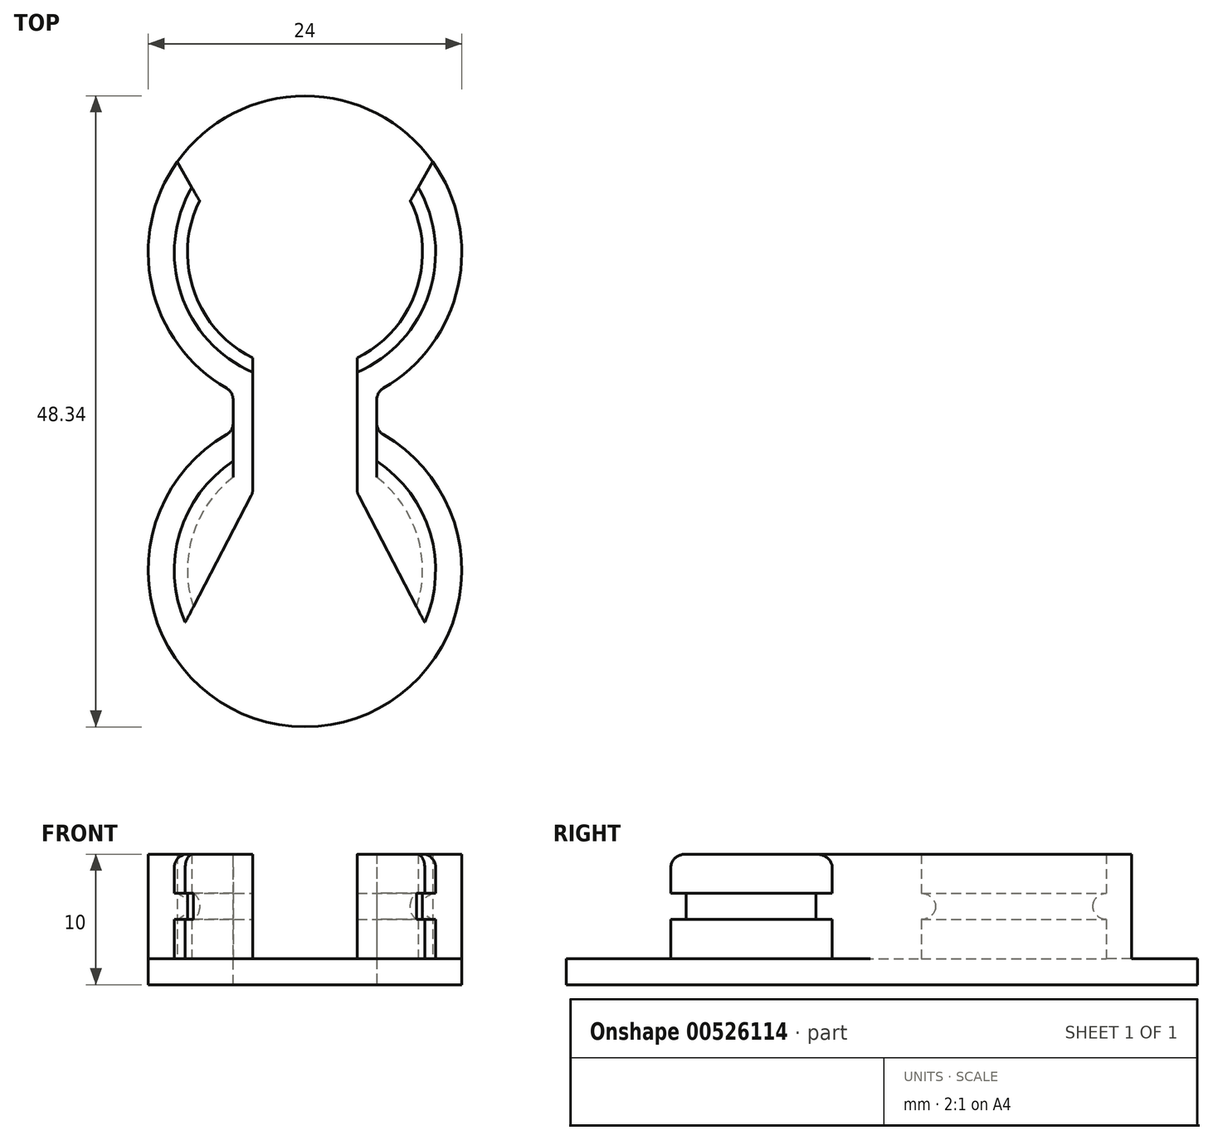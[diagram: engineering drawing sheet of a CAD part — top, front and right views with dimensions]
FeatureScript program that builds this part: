
annotation { "Feature Type Name" : "Feature", "Feature Type Description" : "" }
export const myFeature = defineFeature(function(context is Context, id is Id, definition is map)
    precondition{}
    {
        {
            var Q0;
            Q0=qCreatedBy(makeId("Top.planeOp"),FACE);
            var sketch = newSketch(context, id + "F0", { "sketchPlane" : qUnion([Q0])});
            skArc(sketch, "E0", {"start": v(-5.5, 1.5) * mm, "mid": v(0, 24.17) * mm, "end": v(5.5, 1.5) * mm});
            skArc(sketch, "E1", {"start": v(-5.5, -1.5) * mm, "mid": v(0, -24.17) * mm, "end": v(5.5, -1.5) * mm});
            skLineSegment(sketch, "E2", {"start": v(-5.5, 1.5) * mm, "end": v(-5.5, -1.5) * mm});
            skLineSegment(sketch, "E3", {"start": v(5.5, 1.5) * mm, "end": v(5.5, -1.5) * mm});
            skSolve(sketch);
        }
        {
            var Q0;
            Q0 = qSketchRegion(id + "F0", true);
            extrude(context, id + "F1", {"entities" : qUnion([Q0]), "depth" : 2 * mm, "offsetDistance" : 25 * mm});
        }
        {
            var Q0;
            Q0=makeQuery(id+"F1.opExtrude","CAP_FACE",FACE,{"disambiguationData":[OSD([sQuery(id+"F0.wireOp",EDGE,"E0"),sQuery(id+"F0.wireOp",EDGE,"E1"),sQuery(id+"F0.wireOp",EDGE,"E2"),sQuery(id+"F0.wireOp",EDGE,"E3")])],"isStart":false});
            var sketch = newSketch(context, id + "F2", { "sketchPlane" : qUnion([Q0])});
            skArc(sketch, "E4", {"start": v(8.66, 17.17) * mm, "mid": v(9.5, 9.04) * mm, "end": v(4, 3) * mm});
            skArc(sketch, "E5", {"start": v(9.78, 19.11) * mm, "mid": v(11.66, 9.33) * mm, "end": v(5.5, 1.5) * mm});
            skArc(sketch, "E6", {"start": v(-8.66, 17.17) * mm, "mid": v(-9.5, 9.04) * mm, "end": v(-4, 3) * mm});
            skArc(sketch, "E7", {"start": v(5.5, -3.81) * mm, "mid": v(9.59, -9.32) * mm, "end": v(9.17, -16.17) * mm});
            skLineSegment(sketch, "E8", {"start": v(9.78, 19.11) * mm, "end": v(8.66, 17.17) * mm});
            skLineSegment(sketch, "E9", {"start": v(-8.66, 17.17) * mm, "end": v(-9.78, 19.11) * mm});
            skLineSegment(sketch, "E10", {"start": v(5.5, 1.5) * mm, "end": v(5.5, -3.81) * mm});
            skLineSegment(sketch, "E11", {"start": v(-4, 3) * mm, "end": v(-4, -6.24) * mm});
            skLineSegment(sketch, "E12", {"start": v(-4, -6.24) * mm, "end": v(-9.17, -16.17) * mm});
            skLineSegment(sketch, "E13", {"start": v(9.17, -16.17) * mm, "end": v(4, -6.24) * mm});
            skLineSegment(sketch, "E14", {"start": v(4, -6.24) * mm, "end": v(4, 3) * mm});
            skArc(sketch, "E15", {"start": v(-9.78, 19.11) * mm, "mid": v(-11.66, 9.33) * mm, "end": v(-5.5, 1.5) * mm});
            skArc(sketch, "E16", {"start": v(-9.17, -16.17) * mm, "mid": v(-9.59, -9.32) * mm, "end": v(-5.5, -3.81) * mm});
            skLineSegment(sketch, "E17", {"start": v(-5.5, 1.5) * mm, "end": v(-5.5, -3.81) * mm});
            skArc(sketch, "E18.0", {"start": v(-5.5, 1.5) * mm, "mid": v(0, 24.17) * mm, "end": v(5.5, 1.5) * mm, "construction": true});
            skArc(sketch, "E19.0", {"start": v(-5.5, -1.5) * mm, "mid": v(0, -24.17) * mm, "end": v(5.5, -1.5) * mm, "construction": true});
            skSolve(sketch);
        }
        {
            var Q0;
            Q0 = qSketchRegion(id + "F2", true);
            extrude(context, id + "F3", {"entities" : qUnion([Q0]), "operationType" : NewBodyOperationType.ADD, "depth" : 3 * mm, "offsetDistance" : 25 * mm});
        }
        {
            var Q0;
            Q0=makeQuery(id+"F3.opExtrude","CAP_FACE",FACE,{"disambiguationData":[OSD([sQuery(id+"F2.wireOp",EDGE,"E4"),sQuery(id+"F2.wireOp",EDGE,"E5"),sQuery(id+"F2.wireOp",EDGE,"E7"),sQuery(id+"F2.wireOp",EDGE,"E8"),sQuery(id+"F2.wireOp",EDGE,"E10"),sQuery(id+"F2.wireOp",EDGE,"E13"),sQuery(id+"F2.wireOp",EDGE,"E14")])],"isStart":false});
            var sketch = newSketch(context, id + "F4", { "sketchPlane" : qUnion([Q0])});
            skArc(sketch, "E20", {"start": v(-9.78, 19.11) * mm, "mid": v(-11.66, 9.33) * mm, "end": v(-5.5, 1.5) * mm});
            skArc(sketch, "E21", {"start": v(9.78, 19.11) * mm, "mid": v(11.66, 9.33) * mm, "end": v(5.5, 1.5) * mm});
            skArc(sketch, "E22", {"start": v(8.07, 16.15) * mm, "mid": v(8.53, 9.28) * mm, "end": v(4, 4.1) * mm});
            skArc(sketch, "E23", {"start": v(-8.07, 16.15) * mm, "mid": v(-8.53, 9.28) * mm, "end": v(-4, 4.1) * mm});
            skArc(sketch, "E24", {"start": v(5.5, -5.04) * mm, "mid": v(8.6, -9.53) * mm, "end": v(8.55, -14.98) * mm});
            skArc(sketch, "E25", {"start": v(-5.5, -5.04) * mm, "mid": v(-8.6, -9.53) * mm, "end": v(-8.55, -14.98) * mm});
            skLineSegment(sketch, "E26", {"start": v(-5.5, 1.5) * mm, "end": v(-5.5, -5.04) * mm});
            skLineSegment(sketch, "E27", {"start": v(5.5, 1.5) * mm, "end": v(5.5, -5.04) * mm});
            skLineSegment(sketch, "E28", {"start": v(-4, 4.1) * mm, "end": v(-4, -6.24) * mm});
            skLineSegment(sketch, "E29", {"start": v(-4, -6.24) * mm, "end": v(-8.55, -14.98) * mm});
            skLineSegment(sketch, "E30", {"start": v(4, 4.1) * mm, "end": v(4, -6.24) * mm});
            skLineSegment(sketch, "E31", {"start": v(4, -6.24) * mm, "end": v(8.55, -14.98) * mm});
            skLineSegment(sketch, "E32", {"start": v(8.07, 16.15) * mm, "end": v(9.78, 19.11) * mm});
            skLineSegment(sketch, "E33", {"start": v(-9.78, 19.11) * mm, "end": v(-8.07, 16.15) * mm});
            skLineSegment(sketch, "E34.0", {"start": v(-8.66, 17.17) * mm, "end": v(-9.78, 19.11) * mm, "construction": true});
            skLineSegment(sketch, "E35.0", {"start": v(9.78, 19.11) * mm, "end": v(8.66, 17.17) * mm, "construction": true});
            skLineSegment(sketch, "E36.0", {"start": v(-4, -6.24) * mm, "end": v(-9.17, -16.17) * mm, "construction": true});
            skLineSegment(sketch, "E37.0", {"start": v(9.17, -16.17) * mm, "end": v(4, -6.24) * mm, "construction": true});
            skArc(sketch, "E38.0", {"start": v(-9.78, 19.11) * mm, "mid": v(0, 24.17) * mm, "end": v(9.78, 19.11) * mm, "construction": true});
            skArc(sketch, "E39.0", {"start": v(-5.5, -1.5) * mm, "mid": v(0, -24.17) * mm, "end": v(5.5, -1.5) * mm, "construction": true});
            skSolve(sketch);
        }
        {
            var Q0;
            Q0 = qSketchRegion(id + "F4", true);
            extrude(context, id + "F5", {"entities" : qUnion([Q0]), "operationType" : NewBodyOperationType.ADD, "depth" : 2 * mm, "offsetDistance" : 25 * mm});
        }
        {
            var Q0;
            Q0=makeQuery(id+"F5.opExtrude","CAP_FACE",FACE,{"disambiguationData":[OSD([sQuery(id+"F4.wireOp",EDGE,"E21"),sQuery(id+"F4.wireOp",EDGE,"E22"),sQuery(id+"F4.wireOp",EDGE,"E24"),sQuery(id+"F4.wireOp",EDGE,"E27"),sQuery(id+"F4.wireOp",EDGE,"E30"),sQuery(id+"F4.wireOp",EDGE,"E31"),sQuery(id+"F4.wireOp",EDGE,"E32")])],"isStart":false});
            var sketch = newSketch(context, id + "F6", { "sketchPlane" : qUnion([Q0])});
            skArc(sketch, "E40", {"start": v(8.66, 17.17) * mm, "mid": v(9.5, 9.04) * mm, "end": v(4, 3) * mm});
            skArc(sketch, "E41", {"start": v(9.78, 19.11) * mm, "mid": v(11.66, 9.33) * mm, "end": v(5.5, 1.5) * mm});
            skArc(sketch, "E42", {"start": v(-8.66, 17.17) * mm, "mid": v(-9.5, 9.04) * mm, "end": v(-4, 3) * mm});
            skArc(sketch, "E43", {"start": v(5.5, -3.81) * mm, "mid": v(9.59, -9.32) * mm, "end": v(9.17, -16.17) * mm});
            skLineSegment(sketch, "E44", {"start": v(9.78, 19.11) * mm, "end": v(8.66, 17.17) * mm});
            skLineSegment(sketch, "E45", {"start": v(-8.66, 17.17) * mm, "end": v(-9.78, 19.11) * mm});
            skLineSegment(sketch, "E46", {"start": v(5.5, 1.5) * mm, "end": v(5.5, -3.81) * mm});
            skLineSegment(sketch, "E47", {"start": v(-4, 3) * mm, "end": v(-4, -6.24) * mm});
            skLineSegment(sketch, "E48", {"start": v(-4, -6.24) * mm, "end": v(-9.17, -16.17) * mm});
            skLineSegment(sketch, "E49", {"start": v(9.17, -16.17) * mm, "end": v(4, -6.24) * mm});
            skLineSegment(sketch, "E50", {"start": v(4, -6.24) * mm, "end": v(4, 3) * mm});
            skArc(sketch, "E51", {"start": v(-9.78, 19.11) * mm, "mid": v(-11.66, 9.33) * mm, "end": v(-5.5, 1.5) * mm});
            skArc(sketch, "E52", {"start": v(-9.17, -16.17) * mm, "mid": v(-9.59, -9.32) * mm, "end": v(-5.5, -3.81) * mm});
            skLineSegment(sketch, "E53", {"start": v(-5.5, 1.5) * mm, "end": v(-5.5, -3.81) * mm});
            skArc(sketch, "E54.0", {"start": v(-5.5, -1.5) * mm, "mid": v(0, -24.17) * mm, "end": v(5.5, -1.5) * mm, "construction": true});
            skArc(sketch, "E55.0", {"start": v(-9.78, 19.11) * mm, "mid": v(0, 24.17) * mm, "end": v(9.78, 19.11) * mm, "construction": true});
            skSolve(sketch);
        }
        {
            var Q0;
            Q0 = qSketchRegion(id + "F6", true);
            extrude(context, id + "F7", {"entities" : qUnion([Q0]), "operationType" : NewBodyOperationType.ADD, "depth" : 3 * mm, "offsetDistance" : 25 * mm});
        }
        {
            var Q0;
            Q0=makeQuery(id+"F5.opExtrude","CAP_EDGE",EDGE,{"disambiguationData":[OSD([sQuery(id+"F4.wireOp",EDGE,"E22")])],"isStart":false});
            var Q1;
            Q1=makeQuery(id+"F5.opExtrude","CAP_EDGE",EDGE,{"disambiguationData":[OSD([sQuery(id+"F4.wireOp",EDGE,"E23")])],"isStart":false});
            var Q2;
            Q2=makeQuery(id+"F5.opExtrude","CAP_EDGE",EDGE,{"disambiguationData":[OSD([sQuery(id+"F4.wireOp",EDGE,"E23")])],"isStart":true});
            var Q3;
            Q3=makeQuery(id+"F5.opExtrude","CAP_EDGE",EDGE,{"disambiguationData":[OSD([sQuery(id+"F4.wireOp",EDGE,"E22")])],"isStart":true});
            var Q4;
            Q4=makeQuery(id+"F5.opExtrude","CAP_EDGE",EDGE,{"disambiguationData":[OSD([sQuery(id+"F4.wireOp",EDGE,"E25")])],"isStart":true});
            var Q5;
            Q5=makeQuery(id+"F5.opExtrude","CAP_EDGE",EDGE,{"disambiguationData":[OSD([sQuery(id+"F4.wireOp",EDGE,"E25")])],"isStart":false});
            var Q6;
            Q6=makeQuery(id+"F5.opExtrude","CAP_EDGE",EDGE,{"disambiguationData":[OSD([sQuery(id+"F4.wireOp",EDGE,"E24")])],"isStart":false});
            var Q7;
            Q7=makeQuery(id+"F5.opExtrude","CAP_EDGE",EDGE,{"disambiguationData":[OSD([sQuery(id+"F4.wireOp",EDGE,"E24")])],"isStart":true});
            fillet(context, id + "F8", {"entities" : qUnion([Q0, Q1, Q2, Q3, Q4, Q5, Q6, Q7]), "radius" : 1 * mm, "tangentPropagation" : true, "allowEdgeOverflow" : false});
        }
        {
            var Q0;
            Q0=makeQuery(id+"F3.opExtrude","CAP_EDGE",EDGE,{"disambiguationData":[OSD([sQuery(id+"F2.wireOp",EDGE,"E11")])],"isStart":true});
            var Q1;
            Q1=makeQuery(id+"F3.opExtrude","CAP_EDGE",EDGE,{"disambiguationData":[OSD([sQuery(id+"F2.wireOp",EDGE,"E12")])],"isStart":true});
            var Q2;
            Q2=makeQuery(id+"F7.boolean.opBoolean","MERGE",EDGE,{"derivedFrom":[makeQuery(id+"F5.boolean.opBoolean","MERGE",EDGE,{"derivedFrom":[makeQuery(id+"F3.opExtrude","SWEPT_EDGE",EDGE,{"disambiguationData":[OSD([sQuery(id+"F2.wireOp",EDGE,"E11"),sQuery(id+"F2.wireOp",EDGE,"E12")])]}),makeQuery(id+"F5.opExtrude","SWEPT_EDGE",EDGE,{"disambiguationData":[OSD([sQuery(id+"F4.wireOp",EDGE,"E28"),sQuery(id+"F4.wireOp",EDGE,"E29")])]})]}),makeQuery(id+"F7.opExtrude","SWEPT_EDGE",EDGE,{"disambiguationData":[OSD([sQuery(id+"F6.wireOp",EDGE,"E47"),sQuery(id+"F6.wireOp",EDGE,"E48")])]})]});
            var Q3;
            Q3=makeQuery(id+"F3.opExtrude","CAP_EDGE",EDGE,{"disambiguationData":[OSD([sQuery(id+"F2.wireOp",EDGE,"E13")])],"isStart":true});
            var Q4;
            Q4=makeQuery(id+"F3.opExtrude","CAP_EDGE",EDGE,{"disambiguationData":[OSD([sQuery(id+"F2.wireOp",EDGE,"E14")])],"isStart":true});
            var Q5;
            Q5=makeQuery(id+"F7.boolean.opBoolean","MERGE",EDGE,{"derivedFrom":[makeQuery(id+"F5.boolean.opBoolean","MERGE",EDGE,{"derivedFrom":[makeQuery(id+"F3.opExtrude","SWEPT_EDGE",EDGE,{"disambiguationData":[OSD([sQuery(id+"F2.wireOp",EDGE,"E13"),sQuery(id+"F2.wireOp",EDGE,"E14")])]}),makeQuery(id+"F5.opExtrude","SWEPT_EDGE",EDGE,{"disambiguationData":[OSD([sQuery(id+"F4.wireOp",EDGE,"E30"),sQuery(id+"F4.wireOp",EDGE,"E31")])]})]}),makeQuery(id+"F7.opExtrude","SWEPT_EDGE",EDGE,{"disambiguationData":[OSD([sQuery(id+"F6.wireOp",EDGE,"E49"),sQuery(id+"F6.wireOp",EDGE,"E50")])]})]});
            var Q6;
            Q6=makeQuery(id+"F7.opExtrude","CAP_EDGE",EDGE,{"disambiguationData":[OSD([sQuery(id+"F6.wireOp",EDGE,"E52")])],"isStart":false});
            var Q7;
            Q7=makeQuery(id+"F7.opExtrude","CAP_EDGE",EDGE,{"disambiguationData":[OSD([sQuery(id+"F6.wireOp",EDGE,"E43")])],"isStart":false});
            var Q8;
            Q8=makeQuery(id+"F7.boolean.opBoolean","MERGE",EDGE,{"derivedFrom":[makeQuery(id+"F5.boolean.opBoolean","MERGE",EDGE,{"derivedFrom":[makeQuery(id+"F3.boolean.opBoolean","MERGE",EDGE,{"derivedFrom":[makeQuery(id+"F1.opExtrude","SWEPT_EDGE",EDGE,{"disambiguationData":[OSD([sQuery(id+"F0.wireOp",EDGE,"E0"),sQuery(id+"F0.wireOp",EDGE,"E3")])]}),makeQuery(id+"F3.opExtrude","SWEPT_EDGE",EDGE,{"disambiguationData":[OSD([sQuery(id+"F2.wireOp",EDGE,"E5"),sQuery(id+"F2.wireOp",EDGE,"E10")])]})]}),makeQuery(id+"F5.opExtrude","SWEPT_EDGE",EDGE,{"disambiguationData":[OSD([sQuery(id+"F4.wireOp",EDGE,"E21"),sQuery(id+"F4.wireOp",EDGE,"E27")])]})]}),makeQuery(id+"F7.opExtrude","SWEPT_EDGE",EDGE,{"disambiguationData":[OSD([sQuery(id+"F6.wireOp",EDGE,"E41"),sQuery(id+"F6.wireOp",EDGE,"E46")])]})]});
            var Q9;
            Q9=makeQuery(id+"F1.opExtrude","SWEPT_EDGE",EDGE,{"disambiguationData":[OSD([sQuery(id+"F0.wireOp",EDGE,"E1"),sQuery(id+"F0.wireOp",EDGE,"E3")])]});
            var Q10;
            Q10=makeQuery(id+"F1.opExtrude","SWEPT_EDGE",EDGE,{"disambiguationData":[OSD([sQuery(id+"F0.wireOp",EDGE,"E1"),sQuery(id+"F0.wireOp",EDGE,"E2")])]});
            var Q11;
            Q11=makeQuery(id+"F7.boolean.opBoolean","MERGE",EDGE,{"derivedFrom":[makeQuery(id+"F5.boolean.opBoolean","MERGE",EDGE,{"derivedFrom":[makeQuery(id+"F3.boolean.opBoolean","MERGE",EDGE,{"derivedFrom":[makeQuery(id+"F1.opExtrude","SWEPT_EDGE",EDGE,{"disambiguationData":[OSD([sQuery(id+"F0.wireOp",EDGE,"E0"),sQuery(id+"F0.wireOp",EDGE,"E2")])]}),makeQuery(id+"F3.opExtrude","SWEPT_EDGE",EDGE,{"disambiguationData":[OSD([sQuery(id+"F2.wireOp",EDGE,"E15"),sQuery(id+"F2.wireOp",EDGE,"E17")])]})]}),makeQuery(id+"F5.opExtrude","SWEPT_EDGE",EDGE,{"disambiguationData":[OSD([sQuery(id+"F4.wireOp",EDGE,"E20"),sQuery(id+"F4.wireOp",EDGE,"E26")])]})]}),makeQuery(id+"F7.opExtrude","SWEPT_EDGE",EDGE,{"disambiguationData":[OSD([sQuery(id+"F6.wireOp",EDGE,"E51"),sQuery(id+"F6.wireOp",EDGE,"E53")])]})]});
            fillet(context, id + "F9", {"entities" : qUnion([Q0, Q1, Q2, Q3, Q4, Q5, Q6, Q7, Q8, Q9, Q10, Q11]), "radius" : 1 * mm, "tangentPropagation" : true, "allowEdgeOverflow" : false});
        }
    });
